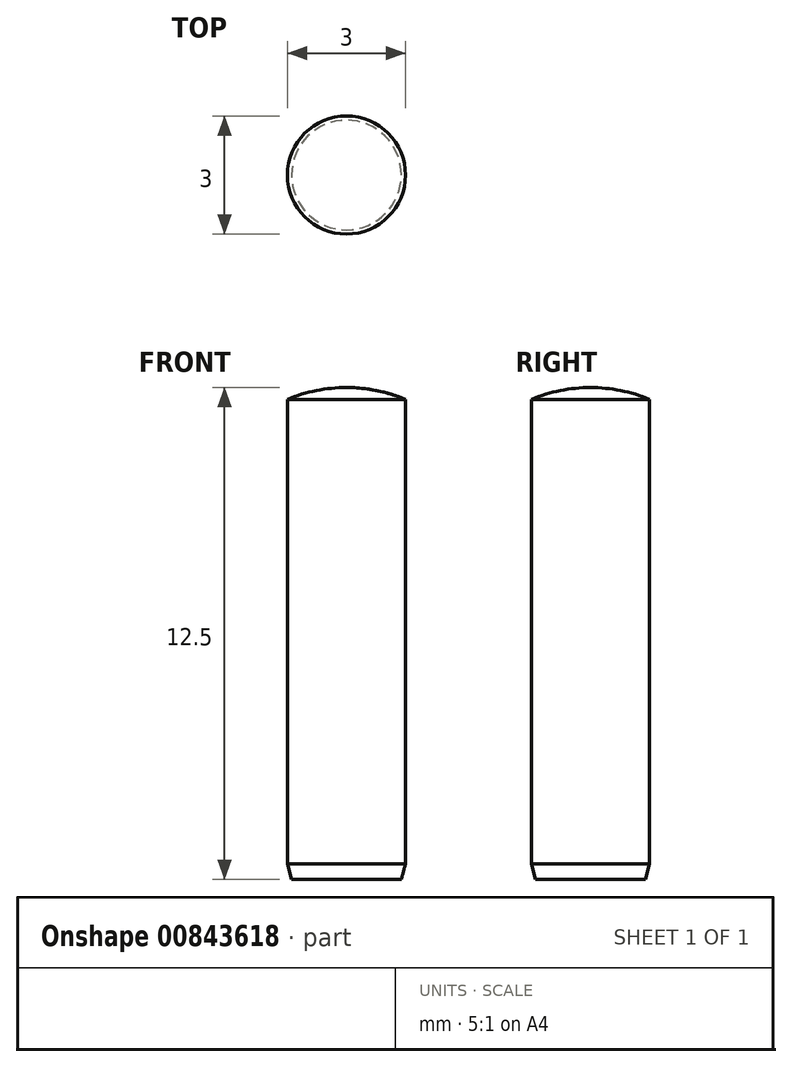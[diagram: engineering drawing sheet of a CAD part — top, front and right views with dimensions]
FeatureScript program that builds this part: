
annotation { "Feature Type Name" : "Feature", "Feature Type Description" : "" }
export const myFeature = defineFeature(function(context is Context, id is Id, definition is map)
    precondition{}
    {
        {
            var Q0;
            Q0=qCreatedBy(makeId("Top.planeOp"),FACE);
            var sketch = newSketch(context, id + "F0", { "sketchPlane" : qUnion([Q0])});
            skCircle(sketch, "E0", {"center": v(0, 0) * mm, "radius": 1.5 * mm});
            skSolve(sketch);
        }
        {
            var Q0;
            Q0=makeQuery(id+"F0.imprint","IMPRINT",FACE,{"disambiguationData":[TD([[makeQuery(id+"F0.imprint","IMPRINT",EDGE,{"derivedFrom":sQuery(id+"F0.wireOp",EDGE,"E0")}),1.0]])]});
            extrude(context, id + "F1", {"entities" : qUnion([Q0]), "depth" : 12.5 * mm, "offsetDistance" : 25 * mm, "symmetric" : true});
        }
        {
            var Q0;
            Q0=qCreatedBy(makeId("Front.planeOp"),FACE);
            var sketch = newSketch(context, id + "F2", { "sketchPlane" : qUnion([Q0])});
            skArc(sketch, "E1", {"start": v(-1.5, 5.95) * mm, "mid": v(-0.76, 6.17) * mm, "end": v(0, 6.25) * mm});
            skPoint(sketch, "E2.endSnap0", {"position": v(0, 6.25) * mm});
            skPoint(sketch, "E3.orphan", {"position": v(1.5, 5.95) * mm});
            skLineSegment(sketch, "E4.top", {"start": v(-1.5, 5.95) * mm, "end": v(-1.66, 5.95) * mm});
            skLineSegment(sketch, "E4.right", {"start": v(-1.66, 6.25) * mm, "end": v(-1.66, 5.95) * mm});
            skLineSegment(sketch, "E5", {"start": v(0, 6.25) * mm, "end": v(0, 0) * mm, "construction": true});
            skLineSegment(sketch, "E6.top", {"start": v(-1.66, 6.35) * mm, "end": v(0, 6.35) * mm});
            skLineSegment(sketch, "E6.left", {"start": v(-1.66, 6.25) * mm, "end": v(-1.66, 6.35) * mm});
            skLineSegment(sketch, "E6.right", {"start": v(0, 6.25) * mm, "end": v(0, 6.35) * mm});
            skPoint(sketch, "E7.start.orphan", {"position": v(-1.5, 6.25) * mm});
            skSolve(sketch);
        }
        {
            var Q0;
            Q0 = qSketchRegion(id + "F2", true);
            var Q1;
            Q1=sQuery(id+"F2.wireOp",EDGE,"E5");
            revolve(context, id + "F3", {"operationType" : NewBodyOperationType.REMOVE, "surfaceOperationType" : NewSurfaceOperationType.NEW, "entities" : qUnion([Q0]), "axis" : qUnion([Q1]), "revolveType" : RevolveType.FULL, "oppositeDirection" : true});
        }
        {
            var Q0;
            Q0=qCreatedBy(makeId("Front.planeOp"),FACE);
            var sketch = newSketch(context, id + "F4", { "sketchPlane" : qUnion([Q0])});
            skLineSegment(sketch, "E8", {"start": v(-1.5, -5.85) * mm, "end": v(-0.93, -7.99) * mm});
            skLineSegment(sketch, "E9", {"start": v(-0.93, -7.99) * mm, "end": v(-1.5, -7.99) * mm});
            skLineSegment(sketch, "E10", {"start": v(-1.5, -7.99) * mm, "end": v(-1.5, -5.85) * mm});
            skLineSegment(sketch, "E11", {"start": v(-1.5, -5.85) * mm, "end": v(1.92, -5.85) * mm, "construction": true});
            skSolve(sketch);
        }
        {
            var Q0;
            Q0=makeQuery(id+"F4.imprint","IMPRINT",FACE,{"disambiguationData":[TD([[makeQuery(id+"F4.imprint","IMPRINT",EDGE,{"derivedFrom":sQuery(id+"F4.wireOp",EDGE,"E8")}),-1.0]])]});
            var Q1;
            Q1=makeQuery(id+"F1.opExtrude","CAP_EDGE",EDGE,{"disambiguationData":[OSD([sQuery(id+"F0.wireOp",EDGE,"E0")])],"isStart":true});
            revolve(context, id + "F5", {"operationType" : NewBodyOperationType.REMOVE, "surfaceOperationType" : NewSurfaceOperationType.NEW, "entities" : qUnion([Q0]), "axis" : qUnion([Q1]), "revolveType" : RevolveType.FULL, "oppositeDirection" : true});
        }
    });
